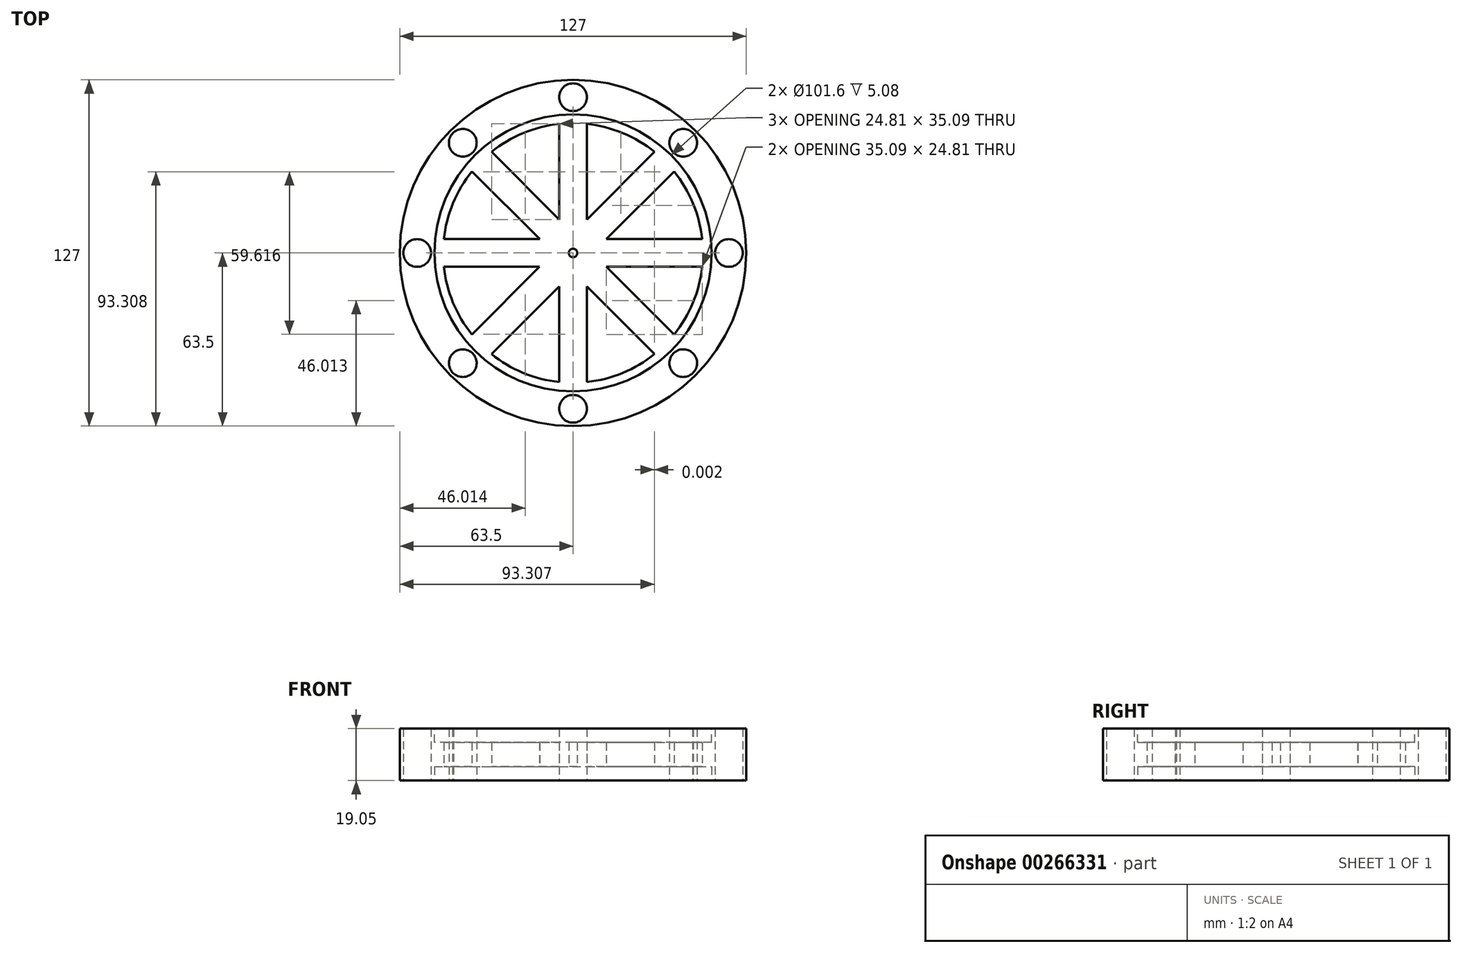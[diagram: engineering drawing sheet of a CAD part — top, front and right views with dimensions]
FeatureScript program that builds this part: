
annotation { "Feature Type Name" : "Feature", "Feature Type Description" : "" }
export const myFeature = defineFeature(function(context is Context, id is Id, definition is map)
    precondition{}
    {
        {
            var Q0;
            Q0=qCreatedBy(makeId("Top.planeOp"),FACE);
            var sketch = newSketch(context, id + "F0", { "sketchPlane" : qUnion([Q0])});
            skArc(sketch, "E0", {"start": v(5.08, -50.55) * mm, "mid": v(19.44, -46.93) * mm, "end": v(32.15, -39.33) * mm});
            skCircle(sketch, "E1", {"center": v(0, 0) * mm, "radius": 1.56 * mm});
            skCircle(sketch, "E2", {"center": v(0, 0) * mm, "radius": 63.5 * mm});
            skPoint(sketch, "E3.start.orphan", {"position": v(-50.8, 0) * mm});
            skPoint(sketch, "E4.end.orphan", {"position": v(1.56, 0) * mm});
            skPoint(sketch, "E4.start.orphan", {"position": v(50.8, 0) * mm});
            skPoint(sketch, "E5.visualSharp", {"position": v(-1.57, 2.58) * mm});
            skPoint(sketch, "E6.visualSharp", {"position": v(1.56, 2.58) * mm});
            skPoint(sketch, "E7.visualSharp", {"position": v(1.56, -2.5) * mm});
            skPoint(sketch, "E8.visualSharp", {"position": v(-1.57, -2.5) * mm});
            skArc(sketch, "E9.trimOffspring", {"start": v(-50.55, -5.08) * mm, "mid": v(-46.93, -19.44) * mm, "end": v(-39.33, -32.15) * mm});
            skArc(sketch, "E10.trimOffspring", {"start": v(50.55, 5.08) * mm, "mid": v(46.93, 19.44) * mm, "end": v(39.33, 32.15) * mm});
            skArc(sketch, "E11.trimOffspring", {"start": v(-5.08, 50.55) * mm, "mid": v(-19.44, 46.93) * mm, "end": v(-32.15, 39.33) * mm});
            skPoint(sketch, "E12.startSnap0", {"position": v(35.56, 36.28) * mm});
            skPoint(sketch, "E12.endSnap0", {"position": v(-35.6, -36.25) * mm});
            skCircle(sketch, "E13", {"center": v(0, 57.15) * mm, "radius": 5.08 * mm});
            skCircle(sketch, "E14.1.0", {"center": v(-40.41, 40.41) * mm, "radius": 5.08 * mm});
            skCircle(sketch, "E14.2.0", {"center": v(-57.15, 0) * mm, "radius": 5.08 * mm});
            skArc(sketch, "E14.3.0", {"start": v(-44.2, -37.03) * mm, "mid": v(-36.82, -44) * mm, "end": v(-43.8, -36.62) * mm});
            skCircle(sketch, "E14.4.0", {"center": v(0, -57.15) * mm, "radius": 5.08 * mm});
            skArc(sketch, "E14.5.0", {"start": v(43.85, -36.68) * mm, "mid": v(36.82, -44) * mm, "end": v(44.15, -36.97) * mm});
            skCircle(sketch, "E15.1.6.0", {"center": v(57.15, 0) * mm, "radius": 5.08 * mm});
            skCircle(sketch, "E15.1.7.0", {"center": v(40.41, 40.41) * mm, "radius": 5.08 * mm});
            skLineSegment(sketch, "E16", {"start": v(44.15, -36.97) * mm, "end": v(43.85, -36.68) * mm});
            skLineSegment(sketch, "E17", {"start": v(-44.2, -37.03) * mm, "end": v(-43.8, -36.62) * mm});
            skLineSegment(sketch, "E18", {"start": v(39.33, 32.15) * mm, "end": v(12.26, 5.08) * mm});
            skPoint(sketch, "E19.orphan", {"position": v(-35.6, -42.78) * mm});
            skLineSegment(sketch, "E20.trimOffspring", {"start": v(-39.33, -32.15) * mm, "end": v(-12.26, -5.08) * mm});
            skLineSegment(sketch, "E21.trimOffspring", {"start": v(39.33, -32.15) * mm, "end": v(12.26, -5.08) * mm});
            skLineSegment(sketch, "E22.trimOffspring", {"start": v(5.08, -12.23) * mm, "end": v(32.15, -39.33) * mm});
            skLineSegment(sketch, "E23.trimOffspring", {"start": v(-5.08, -12.26) * mm, "end": v(-32.15, -39.33) * mm});
            skLineSegment(sketch, "E24.trimOffspring", {"start": v(-5.08, 12.26) * mm, "end": v(-32.15, 39.33) * mm});
            skLineSegment(sketch, "E25.trimOffspring", {"start": v(5.08, 12.26) * mm, "end": v(32.15, 39.33) * mm});
            skLineSegment(sketch, "E26.trimOffspring", {"start": v(-39.3, 32.2) * mm, "end": v(-12.21, 5.08) * mm});
            skLineSegment(sketch, "E27", {"start": v(-5.08, 50.55) * mm, "end": v(-5.08, 12.26) * mm});
            skLineSegment(sketch, "E28", {"start": v(5.08, -50.55) * mm, "end": v(5.08, -12.23) * mm});
            skLineSegment(sketch, "E29.trimOffspring", {"start": v(-5.08, -12.26) * mm, "end": v(-5.08, -50.55) * mm});
            skLineSegment(sketch, "E30.trimOffspring", {"start": v(5.08, 12.26) * mm, "end": v(5.08, 50.55) * mm});
            skArc(sketch, "E31.trimOffspring", {"start": v(-39.3, 32.2) * mm, "mid": v(-46.92, 19.47) * mm, "end": v(-50.55, 5.08) * mm});
            skArc(sketch, "E32.trimOffspring", {"start": v(-32.15, -39.33) * mm, "mid": v(-19.44, -46.93) * mm, "end": v(-5.08, -50.55) * mm});
            skArc(sketch, "E33.trimOffspring", {"start": v(32.15, 39.33) * mm, "mid": v(19.44, 46.93) * mm, "end": v(5.08, 50.55) * mm});
            skArc(sketch, "E34.trimOffspring", {"start": v(39.33, -32.15) * mm, "mid": v(46.93, -19.44) * mm, "end": v(50.55, -5.08) * mm});
            skLineSegment(sketch, "E35", {"start": v(-50.55, 5.08) * mm, "end": v(-12.21, 5.08) * mm});
            skLineSegment(sketch, "E36", {"start": v(-50.55, -5.08) * mm, "end": v(-12.26, -5.08) * mm});
            skLineSegment(sketch, "E37.trimOffspring", {"start": v(12.26, 5.08) * mm, "end": v(50.55, 5.08) * mm});
            skLineSegment(sketch, "E38.trimOffspring", {"start": v(12.26, -5.08) * mm, "end": v(50.55, -5.08) * mm});
            skArc(sketch, "E39", {"start": v(29.9, 37.08) * mm, "mid": v(18.23, 44) * mm, "end": v(5.08, 47.35) * mm});
            skArc(sketch, "E40.trimOffspring", {"start": v(-5.08, 47.35) * mm, "mid": v(-18.23, 44) * mm, "end": v(-29.9, 37.08) * mm});
            skArc(sketch, "E41.trimOffspring", {"start": v(-37.04, 29.94) * mm, "mid": v(-43.99, 18.25) * mm, "end": v(-47.35, 5.08) * mm});
            skArc(sketch, "E42.trimOffspring", {"start": v(-47.35, -5.08) * mm, "mid": v(-44, -18.23) * mm, "end": v(-37.07, -29.9) * mm});
            skArc(sketch, "E43.trimOffspring", {"start": v(-29.9, -37.08) * mm, "mid": v(0, -47.62) * mm, "end": v(29.9, -37.07) * mm});
            skArc(sketch, "E44.trimOffspring", {"start": v(37.07, -29.9) * mm, "mid": v(44, -18.23) * mm, "end": v(47.35, -5.08) * mm});
            skArc(sketch, "E45.trimOffspring", {"start": v(47.35, 5.08) * mm, "mid": v(44, 18.23) * mm, "end": v(37.08, 29.9) * mm});
            skSolve(sketch);
        }
        {
            var Q0;
            Q0=makeQuery(id+"F0.imprint","IMPRINT",FACE,{"disambiguationData":[TD([[makeQuery(id+"F0.imprint","IMPRINT",EDGE,{"derivedFrom":sQuery(id+"F0.wireOp",EDGE,"E0")}),-1.0]])]});
            var Q1;
            {var subQ0=sQuery(id+"F0.wireOp",EDGE,"E31.trimOffspring");Q1=makeQuery(id+"F0.imprint","IMPRINT",FACE,{"disambiguationData":[TD([[makeQuery(id+"F0.imprint","IMPRINT",EDGE,{"derivedFrom":subQ0}),1.0]])]});}
            var Q2;
            {var subQ0=sQuery(id+"F0.wireOp",EDGE,"E11.trimOffspring");Q2=makeQuery(id+"F0.imprint","IMPRINT",FACE,{"disambiguationData":[TD([[makeQuery(id+"F0.imprint","IMPRINT",EDGE,{"derivedFrom":subQ0}),1.0]])]});}
            var Q3;
            {var subQ0=sQuery(id+"F0.wireOp",EDGE,"E9.trimOffspring");Q3=makeQuery(id+"F0.imprint","IMPRINT",FACE,{"disambiguationData":[TD([[makeQuery(id+"F0.imprint","IMPRINT",EDGE,{"derivedFrom":subQ0}),1.0]])]});}
            var Q4;
            {var subQ0=sQuery(id+"F0.wireOp",EDGE,"E32.trimOffspring");Q4=makeQuery(id+"F0.imprint","IMPRINT",FACE,{"disambiguationData":[TD([[makeQuery(id+"F0.imprint","IMPRINT",EDGE,{"derivedFrom":subQ0}),1.0]])]});}
            var Q5;
            {var subQ0=sQuery(id+"F0.wireOp",EDGE,"E0");Q5=makeQuery(id+"F0.imprint","IMPRINT",FACE,{"disambiguationData":[TD([[makeQuery(id+"F0.imprint","IMPRINT",EDGE,{"derivedFrom":subQ0}),1.0]])]});}
            var Q6;
            {var subQ0=sQuery(id+"F0.wireOp",EDGE,"E34.trimOffspring");Q6=makeQuery(id+"F0.imprint","IMPRINT",FACE,{"disambiguationData":[TD([[makeQuery(id+"F0.imprint","IMPRINT",EDGE,{"derivedFrom":subQ0}),1.0]])]});}
            var Q7;
            {var subQ0=sQuery(id+"F0.wireOp",EDGE,"E10.trimOffspring");Q7=makeQuery(id+"F0.imprint","IMPRINT",FACE,{"disambiguationData":[TD([[makeQuery(id+"F0.imprint","IMPRINT",EDGE,{"derivedFrom":subQ0}),1.0]])]});}
            var Q8;
            {var subQ0=sQuery(id+"F0.wireOp",EDGE,"E33.trimOffspring");Q8=makeQuery(id+"F0.imprint","IMPRINT",FACE,{"disambiguationData":[TD([[makeQuery(id+"F0.imprint","IMPRINT",EDGE,{"derivedFrom":subQ0}),1.0]])]});}
            extrude(context, id + "F1", {"entities" : qUnion([Q0, Q1, Q2, Q3, Q4, Q5, Q6, Q7, Q8]), "depth" : 19.05 * mm});
        }
        {
            var Q0;
            Q0=makeQuery(id+"F1.opExtrude","CAP_FACE",FACE,{"disambiguationData":[OSD([sQuery(id+"F0.wireOp",EDGE,"E0"),sQuery(id+"F0.wireOp",EDGE,"E1"),sQuery(id+"F0.wireOp",EDGE,"E2"),sQuery(id+"F0.wireOp",EDGE,"88hn0kWC-duqa-wjVB-21yq-hkDgDDczfLqz"),sQuery(id+"F0.wireOp",EDGE,"ama5MNr1-txNQ-iBb5-azgy-jXuDfxf7aiFx"),sQuery(id+"F0.wireOp",EDGE,"maItcgYP-eVuS-LiKE-Hy4X-MGX7yfKcc9Bj"),sQuery(id+"F0.wireOp",EDGE,"75kgPRwH-r0TD-Qq4O-Chhf-XQQBpnsMARJg"),sQuery(id+"F0.wireOp",EDGE,"E9.trimOffspring"),sQuery(id+"F0.wireOp",EDGE,"E10.trimOffspring"),sQuery(id+"F0.wireOp",EDGE,"E11.trimOffspring"),sQuery(id+"F0.wireOp",EDGE,"a337ef4f-a6b8-49e8-bdae-0f163152fc78.trimOffspring"),sQuery(id+"F0.wireOp",EDGE,"6ddb9681-1824-4842-a86d-73ac6b74ed59.trimOffspring"),sQuery(id+"F0.wireOp",EDGE,"04f78fd6-2a0e-4e57-9acc-05abb21af257.trimOffspring"),sQuery(id+"F0.wireOp",EDGE,"506943a0-4222-43f1-9abc-ef08afb6956f.trimOffspring"),sQuery(id+"F0.wireOp",EDGE,"E13"),sQuery(id+"F0.wireOp",EDGE,"E14.1.0"),sQuery(id+"F0.wireOp",EDGE,"E14.2.0"),sQuery(id+"F0.wireOp",EDGE,"E14.3.0"),sQuery(id+"F0.wireOp",EDGE,"E14.4.0"),sQuery(id+"F0.wireOp",EDGE,"E14.5.0"),sQuery(id+"F0.wireOp",EDGE,"WVwh1Rsb-04Ei-j4m1-iXqr-hOYMxM5rheej"),sQuery(id+"F0.wireOp",EDGE,"E15.1.6.0"),sQuery(id+"F0.wireOp",EDGE,"E15.1.7.0"),sQuery(id+"F0.wireOp",EDGE,"E16"),sQuery(id+"F0.wireOp",EDGE,"E17"),sQuery(id+"F0.wireOp",EDGE,"E18"),sQuery(id+"F0.wireOp",EDGE,"E20.trimOffspring"),sQuery(id+"F0.wireOp",EDGE,"E21.trimOffspring"),sQuery(id+"F0.wireOp",EDGE,"E22.trimOffspring"),sQuery(id+"F0.wireOp",EDGE,"E23.trimOffspring"),sQuery(id+"F0.wireOp",EDGE,"E24.trimOffspring"),sQuery(id+"F0.wireOp",EDGE,"E25.trimOffspring"),sQuery(id+"F0.wireOp",EDGE,"E26.trimOffspring"),sQuery(id+"F0.wireOp",EDGE,"L11nAbpQ-mLoI-7c1p-HgbM-ncSsEOqsixXA"),sQuery(id+"F0.wireOp",EDGE,"ZsSWKLiw-0hpN-u02Z-UbGG-FH6ZjaUcbqHe"),sQuery(id+"F0.wireOp",EDGE,"Puo8Kbwl-Vwbr-lQFv-Rnjq-q6n5ii1xTP1v"),sQuery(id+"F0.wireOp",EDGE,"STJF5vwg-Zvhj-BZAk-nIep-njkhL0idrNQy"),sQuery(id+"F0.wireOp",EDGE,"E27"),sQuery(id+"F0.wireOp",EDGE,"E28"),sQuery(id+"F0.wireOp",EDGE,"E29.trimOffspring"),sQuery(id+"F0.wireOp",EDGE,"E30.trimOffspring"),sQuery(id+"F0.wireOp",EDGE,"E31.trimOffspring"),sQuery(id+"F0.wireOp",EDGE,"E32.trimOffspring"),sQuery(id+"F0.wireOp",EDGE,"E33.trimOffspring"),sQuery(id+"F0.wireOp",EDGE,"E34.trimOffspring")])],"isStart":true});
            var sketch = newSketch(context, id + "F2", { "sketchPlane" : qUnion([Q0])});
            skCircle(sketch, "E46", {"center": v(0, 0) * mm, "radius": 50.8 * mm});
            skSolve(sketch);
        }
        {
            var Q0;
            Q0=makeQuery(id+"F2.imprint","IMPRINT",FACE,{"disambiguationData":[TD([[makeQuery(id+"F2.imprint","IMPRINT",EDGE,{"derivedFrom":makeQuery(id+"F1.opExtrude","CAP_EDGE",EDGE,{"disambiguationData":[OSD([sQuery(id+"F0.wireOp",EDGE,"E1")])],"isStart":true})}),1.0]])]});
            extrude(context, id + "F3", {"entities" : qUnion([Q0]), "operationType" : NewBodyOperationType.REMOVE, "oppositeDirection" : true, "depth" : 5.08 * mm});
        }
        {
            var Q0;
            Q0=makeQuery(id+"F1.opExtrude","CAP_FACE",FACE,{"disambiguationData":[OSD([sQuery(id+"F0.wireOp",EDGE,"E0"),sQuery(id+"F0.wireOp",EDGE,"E1"),sQuery(id+"F0.wireOp",EDGE,"E2"),sQuery(id+"F0.wireOp",EDGE,"88hn0kWC-duqa-wjVB-21yq-hkDgDDczfLqz"),sQuery(id+"F0.wireOp",EDGE,"ama5MNr1-txNQ-iBb5-azgy-jXuDfxf7aiFx"),sQuery(id+"F0.wireOp",EDGE,"maItcgYP-eVuS-LiKE-Hy4X-MGX7yfKcc9Bj"),sQuery(id+"F0.wireOp",EDGE,"75kgPRwH-r0TD-Qq4O-Chhf-XQQBpnsMARJg"),sQuery(id+"F0.wireOp",EDGE,"E9.trimOffspring"),sQuery(id+"F0.wireOp",EDGE,"E10.trimOffspring"),sQuery(id+"F0.wireOp",EDGE,"E11.trimOffspring"),sQuery(id+"F0.wireOp",EDGE,"a337ef4f-a6b8-49e8-bdae-0f163152fc78.trimOffspring"),sQuery(id+"F0.wireOp",EDGE,"6ddb9681-1824-4842-a86d-73ac6b74ed59.trimOffspring"),sQuery(id+"F0.wireOp",EDGE,"04f78fd6-2a0e-4e57-9acc-05abb21af257.trimOffspring"),sQuery(id+"F0.wireOp",EDGE,"506943a0-4222-43f1-9abc-ef08afb6956f.trimOffspring"),sQuery(id+"F0.wireOp",EDGE,"E13"),sQuery(id+"F0.wireOp",EDGE,"E14.1.0"),sQuery(id+"F0.wireOp",EDGE,"E14.2.0"),sQuery(id+"F0.wireOp",EDGE,"E14.3.0"),sQuery(id+"F0.wireOp",EDGE,"E14.4.0"),sQuery(id+"F0.wireOp",EDGE,"E14.5.0"),sQuery(id+"F0.wireOp",EDGE,"WVwh1Rsb-04Ei-j4m1-iXqr-hOYMxM5rheej"),sQuery(id+"F0.wireOp",EDGE,"E15.1.6.0"),sQuery(id+"F0.wireOp",EDGE,"E15.1.7.0"),sQuery(id+"F0.wireOp",EDGE,"E16"),sQuery(id+"F0.wireOp",EDGE,"E17"),sQuery(id+"F0.wireOp",EDGE,"E18"),sQuery(id+"F0.wireOp",EDGE,"E20.trimOffspring"),sQuery(id+"F0.wireOp",EDGE,"E21.trimOffspring"),sQuery(id+"F0.wireOp",EDGE,"E22.trimOffspring"),sQuery(id+"F0.wireOp",EDGE,"E23.trimOffspring"),sQuery(id+"F0.wireOp",EDGE,"E24.trimOffspring"),sQuery(id+"F0.wireOp",EDGE,"E25.trimOffspring"),sQuery(id+"F0.wireOp",EDGE,"E26.trimOffspring"),sQuery(id+"F0.wireOp",EDGE,"L11nAbpQ-mLoI-7c1p-HgbM-ncSsEOqsixXA"),sQuery(id+"F0.wireOp",EDGE,"ZsSWKLiw-0hpN-u02Z-UbGG-FH6ZjaUcbqHe"),sQuery(id+"F0.wireOp",EDGE,"Puo8Kbwl-Vwbr-lQFv-Rnjq-q6n5ii1xTP1v"),sQuery(id+"F0.wireOp",EDGE,"STJF5vwg-Zvhj-BZAk-nIep-njkhL0idrNQy"),sQuery(id+"F0.wireOp",EDGE,"E27"),sQuery(id+"F0.wireOp",EDGE,"E28"),sQuery(id+"F0.wireOp",EDGE,"E29.trimOffspring"),sQuery(id+"F0.wireOp",EDGE,"E30.trimOffspring"),sQuery(id+"F0.wireOp",EDGE,"E31.trimOffspring"),sQuery(id+"F0.wireOp",EDGE,"E32.trimOffspring"),sQuery(id+"F0.wireOp",EDGE,"E33.trimOffspring"),sQuery(id+"F0.wireOp",EDGE,"E34.trimOffspring")])],"isStart":false});
            var sketch = newSketch(context, id + "F4", { "sketchPlane" : qUnion([Q0])});
            skCircle(sketch, "E47", {"center": v(0, 0) * mm, "radius": 50.8 * mm});
            skSolve(sketch);
        }
        {
            var Q0;
            Q0=makeQuery(id+"F4.imprint","IMPRINT",FACE,{"disambiguationData":[TD([[makeQuery(id+"F4.imprint","IMPRINT",EDGE,{"derivedFrom":makeQuery(id+"F1.opExtrude","CAP_EDGE",EDGE,{"disambiguationData":[OSD([sQuery(id+"F0.wireOp",EDGE,"E1")])],"isStart":false})}),-1.0]])]});
            extrude(context, id + "F5", {"entities" : qUnion([Q0]), "operationType" : NewBodyOperationType.REMOVE, "oppositeDirection" : true, "depth" : 5.08 * mm});
        }
    });
